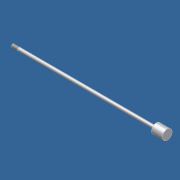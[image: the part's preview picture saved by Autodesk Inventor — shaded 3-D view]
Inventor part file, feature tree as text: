
AUTODESK INVENTOR PART (.ipt)
format: ipt  version: 2012 (Build 160160000, 160)  size: 124,416 bytes
history: native  units: in
note: dims shown in document units (in); Inventor stores cm internally (conversion verified against a paired STEP export)
features: other x84, revolve x3, sketch x3, thread x1
ambient origin geometry x8: Origin, YZ Plane, XZ Plane, XY Plane, X Axis, Y Axis, Z Axis, Center Point
bodies: Solid1 (feature_tree)
feature tree (91):
  revolve  "Revolution1"  Angle=360.0deg
  revolve  "Revolution2"  Angle=360.0deg
  thread  "Thread1"  [1 undecoded]
  revolve  "Revolution3"  [1 undecoded]
  other  "rod_cp_XY"
  other  "rod_cp_YZ"
  other  "rod_cp_ZX"
  other  "rod_cp_X"
  other  "rod_cp_Y"
  other  "rod_cp_Z"
  other  "rod_cp_Center"
  other  "to_rod_clevis_XY"
  other  "to_rod_clevis_YZ"
  other  "to_rod_clevis_ZX"
  other  "to_rod_clevis_X"
  other  "to_rod_clevis_Y"
  other  "to_rod_clevis_Z"
  other  "to_rod_clevis_Center"
  other  "rl2_XY"
  other  "rl2_YZ"
  other  "rl2_ZX"
  other  "rl2_X"
  other  "rl2_Y"
  other  "rl2_Z"
  other  "rl2_Center"
  other  "rl1_XY"
  other  "rl1_YZ"
  other  "rl1_ZX"
  other  "rl1_X"
  other  "rl1_Y"
  other  "rl1_Z"
  other  "rl1_Center"
  other  "thd1_XY"
  other  "thd1_YZ"
  other  "thd1_ZX"
  other  "thd1_X"
  other  "thd1_Y"
  other  "thd1_Z"
  other  "thd1_Center"
  other  "thd2_XY"
  other  "thd2_YZ"
  other  "thd2_ZX"
  other  "thd2_X"
  other  "thd2_Y"
  other  "thd2_Z"
  other  "thd2_Center"
  other  "dia1_XY"
  other  "dia1_YZ"
  other  "dia1_ZX"
  other  "dia1_X"
  other  "dia1_Y"
  other  "dia1_Z"
  other  "dia1_Center"
  other  "dia2_XY"
  other  "dia2_YZ"
  other  "dia2_ZX"
  other  "dia2_X"
  other  "dia2_Y"
  other  "dia2_Z"
  other  "dia2_Center"
  other  "hh1_XY"
  other  "hh1_YZ"
  other  "hh1_ZX"
  other  "hh1_X"
  other  "hh1_Y"
  other  "hh1_Z"
  other  "hh1_Center"
  other  "hh2_XY"
  other  "hh2_YZ"
  other  "hh2_ZX"
  other  "hh2_X"
  other  "hh2_Y"
  other  "hh2_Z"
  other  "hh2_Center"
  other  "dia12_XY"
  other  "dia12_YZ"
  other  "dia12_ZX"
  other  "dia12_X"
  other  "dia12_Y"
  other  "dia12_Z"
  other  "dia12_Center"
  other  "dia22_XY"
  other  "dia22_YZ"
  other  "dia22_ZX"
  other  "dia22_X"
  other  "dia22_Y"
  other  "dia22_Z"
  other  "dia22_Center"
  sketch  "Sketch_1"  dims[d0=360.0deg d1=360.0deg]
  sketch  "Sketch_3"  dims[d2=0.5in d3=10.594in d4=360.0deg]
  sketch  "Sketch_30"
note: 2 required parameter values undecoded (feature->parameter linkage not recoverable at this tier; creation-order binding heuristic only, values carry confidence <= 0.55)
